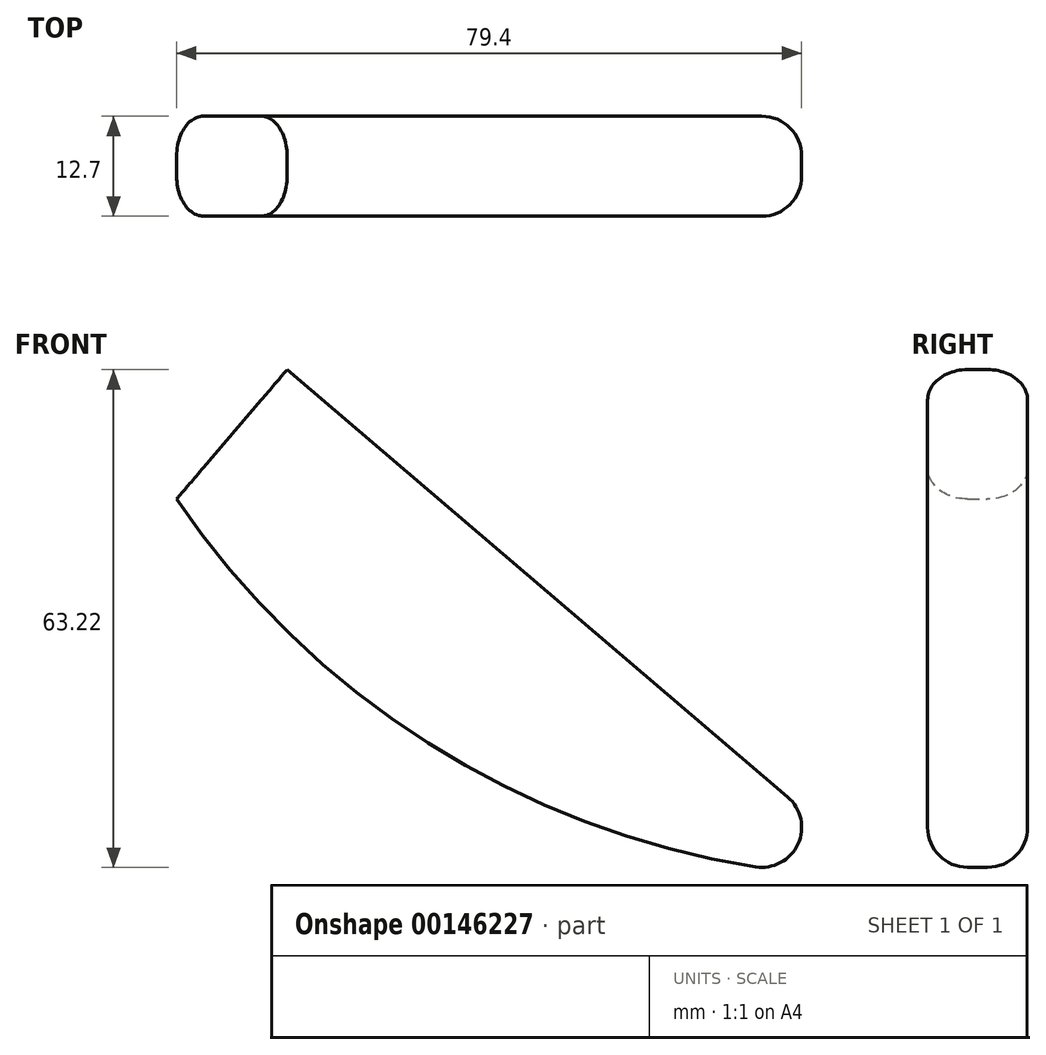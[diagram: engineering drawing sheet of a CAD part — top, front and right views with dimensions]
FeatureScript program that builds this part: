
annotation { "Feature Type Name" : "Feature", "Feature Type Description" : "" }
export const myFeature = defineFeature(function(context is Context, id is Id, definition is map)
    precondition{}
    {
        {
            var Q0;
            Q0=qCreatedBy(makeId("Front.planeOp"),FACE);
            var sketch = newSketch(context, id + "F0", { "sketchPlane" : qUnion([Q0])});
            skLineSegment(sketch, "E0", {"start": v(-34.02, 36.9) * mm, "end": v(41.53, -27.62) * mm});
            skLineSegment(sketch, "E1", {"start": v(-34.02, 36.9) * mm, "end": v(-48.06, 20.46) * mm});
            skArc(sketch, "E2", {"start": v(-48.06, 20.46) * mm, "mid": v(-9.18, -14.6) * mm, "end": v(41.53, -27.62) * mm});
            skSolve(sketch);
        }
        {
            var Q0;
            Q0=makeQuery(id+"F0.imprint","IMPRINT",FACE,{"disambiguationData":[TD([[makeQuery(id+"F0.imprint","IMPRINT",EDGE,{"derivedFrom":sQuery(id+"F0.wireOp",EDGE,"E0")}),-1.0]])]});
            extrude(context, id + "F1", {"entities" : qUnion([Q0]), "depth" : 12.7 * mm});
        }
        {
            var Q0;
            Q0=makeQuery(id+"F1.opExtrude","CAP_EDGE",EDGE,{"disambiguationData":[OSD([sQuery(id+"F0.wireOp",EDGE,"E0")])],"isStart":false});
            var Q1;
            Q1=makeQuery(id+"F1.opExtrude","CAP_EDGE",EDGE,{"disambiguationData":[OSD([sQuery(id+"F0.wireOp",EDGE,"E2")])],"isStart":false});
            var Q2;
            Q2=makeQuery(id+"F1.opExtrude","CAP_EDGE",EDGE,{"disambiguationData":[OSD([sQuery(id+"F0.wireOp",EDGE,"E2")])],"isStart":true});
            var Q3;
            Q3=makeQuery(id+"F1.opExtrude","CAP_EDGE",EDGE,{"disambiguationData":[OSD([sQuery(id+"F0.wireOp",EDGE,"E0")])],"isStart":true});
            var Q4;
            Q4=makeQuery(id+"F1.opExtrude","SWEPT_EDGE",EDGE,{"disambiguationData":[OSD([sQuery(id+"F0.wireOp",EDGE,"E0"),sQuery(id+"F0.wireOp",EDGE,"E2")])]});
            fillet(context, id + "F2", {"entities" : qUnion([Q0, Q1, Q2, Q3, Q4]), "radius" : 5.08 * mm, "tangentPropagation" : true, "allowEdgeOverflow" : false});
        }
    });
